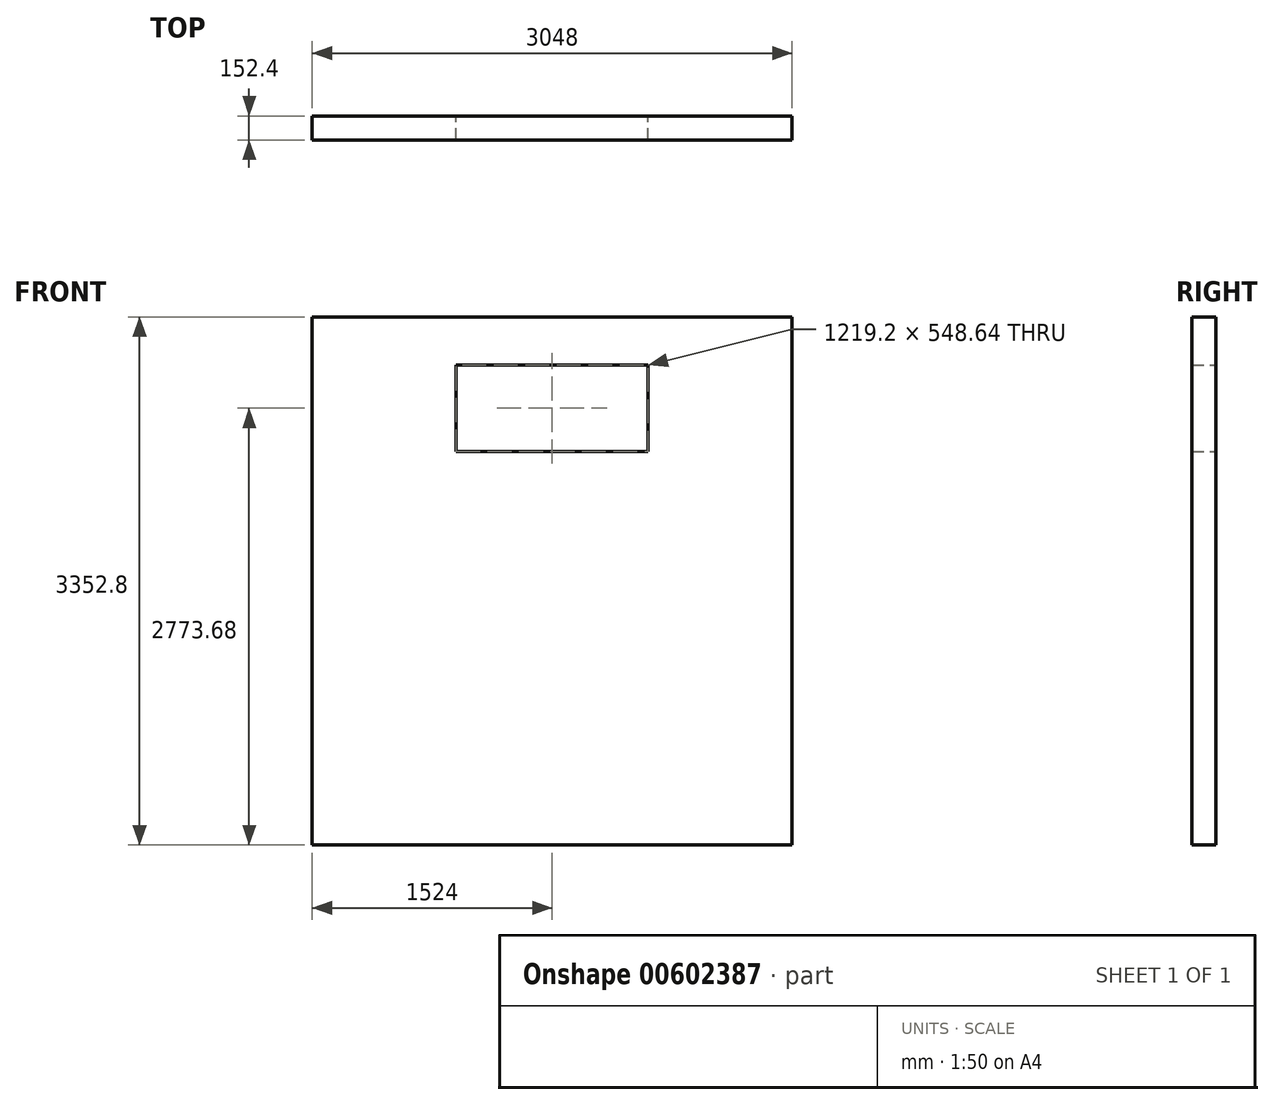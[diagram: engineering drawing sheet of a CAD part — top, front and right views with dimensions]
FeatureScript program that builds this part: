
annotation { "Feature Type Name" : "Feature", "Feature Type Description" : "" }
export const myFeature = defineFeature(function(context is Context, id is Id, definition is map)
    precondition{}
    {
        {
            var Q0;
            Q0=qCreatedBy(makeId("Front.planeOp"),FACE);
            var sketch = newSketch(context, id + "F0", { "sketchPlane" : qUnion([Q0])});
            skLineSegment(sketch, "E0.bottom", {"start": v(-1524, 1676.4) * mm, "end": v(1524, 1676.4) * mm});
            skLineSegment(sketch, "E0.top", {"start": v(-1524, -1676.4) * mm, "end": v(1524, -1676.4) * mm});
            skLineSegment(sketch, "E0.left", {"start": v(-1524, 1676.4) * mm, "end": v(-1524, -1676.4) * mm});
            skLineSegment(sketch, "E0.right", {"start": v(1524, 1676.4) * mm, "end": v(1524, -1676.4) * mm});
            skPoint(sketch, "E0.middle", {"position": v(0, 0) * mm});
            skLineSegment(sketch, "E1.bottom", {"start": v(-609.6, 1371.6) * mm, "end": v(609.6, 1371.6) * mm});
            skLineSegment(sketch, "E1.top", {"start": v(-609.6, 822.96) * mm, "end": v(609.6, 822.96) * mm});
            skLineSegment(sketch, "E1.left", {"start": v(-609.6, 1371.6) * mm, "end": v(-609.6, 822.96) * mm});
            skLineSegment(sketch, "E1.right", {"start": v(609.6, 1371.6) * mm, "end": v(609.6, 822.96) * mm});
            skPoint(sketch, "E1.middle", {"position": v(0, 1097.28) * mm});
            skSolve(sketch);
        }
        {
            var Q0;
            Q0=makeQuery(id+"F0.imprint","IMPRINT",FACE,{"disambiguationData":[TD([[makeQuery(id+"F0.imprint","IMPRINT",EDGE,{"derivedFrom":sQuery(id+"F0.wireOp",EDGE,"E0.bottom")}),-1.0]])]});
            extrude(context, id + "F1", {"entities" : qUnion([Q0]), "depth" : 152.4 * mm, "offsetDistance" : 30.48 * mm});
        }
    });
